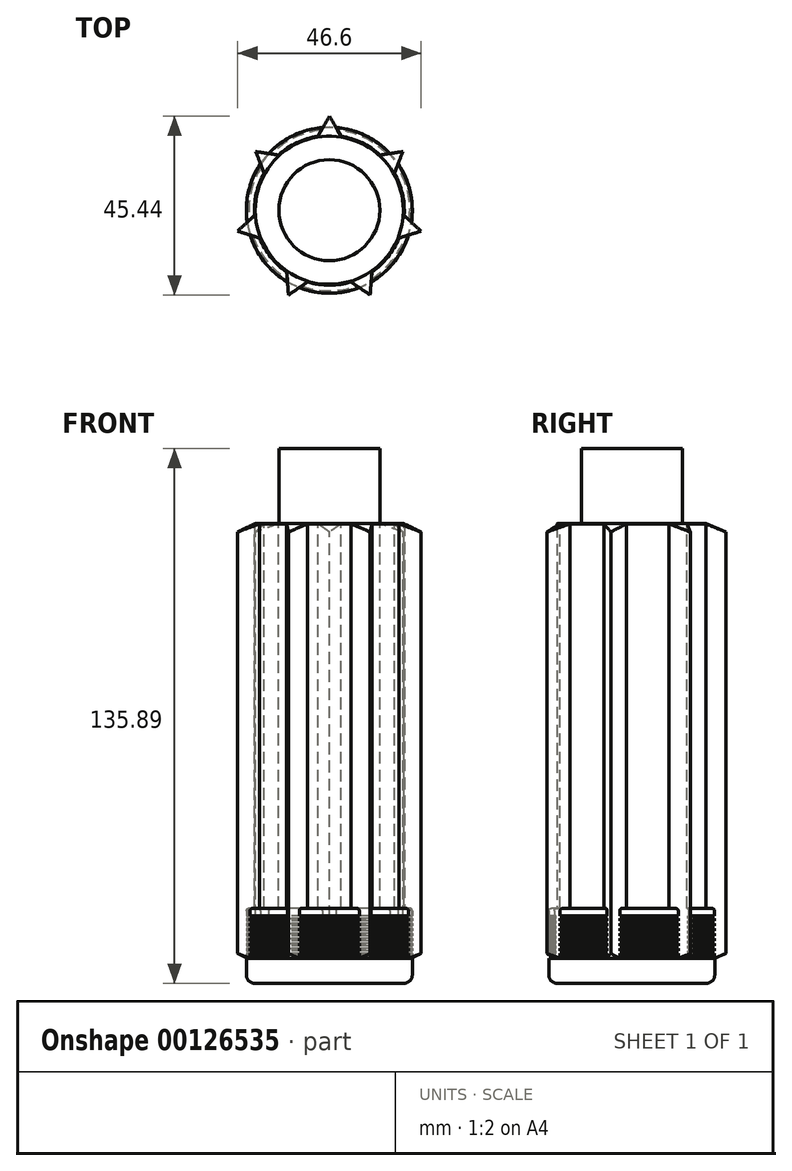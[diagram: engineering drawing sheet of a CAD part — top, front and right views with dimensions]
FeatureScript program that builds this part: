
annotation { "Feature Type Name" : "Feature", "Feature Type Description" : "" }
export const myFeature = defineFeature(function(context is Context, id is Id, definition is map)
    precondition{}
    {
        {
            var Q0;
            Q0=qCreatedBy(makeId("Top.planeOp"),FACE);
            var sketch = newSketch(context, id + "F0", { "sketchPlane" : qUnion([Q0])});
            skCircle(sketch, "E0", {"center": v(0, 0) * mm, "radius": 19.05 * mm});
            skSolve(sketch);
        }
        {
            var Q0;
            Q0 = qSketchRegion(id + "F0", true);
            extrude(context, id + "F1", {"entities" : qUnion([Q0]), "depth" : 116.84 * mm});
        }
        {
            var Q0;
            Q0=qCreatedBy(makeId("Top.planeOp"),FACE);
            var sketch = newSketch(context, id + "F2", { "sketchPlane" : qUnion([Q0])});
            skCircle(sketch, "E1.0", {"center": v(0, 0) * mm, "radius": 21.08 * mm});
            skSolve(sketch);
        }
        {
            var Q0;
            Q0 = qSketchRegion(id + "F2", true);
            extrude(context, id + "F3", {"entities" : qUnion([Q0]), "operationType" : NewBodyOperationType.ADD, "depth" : 19.05 * mm});
        }
        {
            var Q0;
            Q0=qCreatedBy(makeId("Front.planeOp"),FACE);
            var sketch = newSketch(context, id + "F4", { "sketchPlane" : qUnion([Q0])});
            skLineSegment(sketch, "E2.bottom", {"start": v(-21.08, 6.4) * mm, "end": v(-20.45, 6.4) * mm});
            skLineSegment(sketch, "E2.top", {"start": v(-21.08, 7.03) * mm, "end": v(-20.45, 7.03) * mm});
            skLineSegment(sketch, "E2.left", {"start": v(-21.08, 6.4) * mm, "end": v(-21.08, 7.03) * mm});
            skLineSegment(sketch, "E2.right", {"start": v(-20.45, 6.4) * mm, "end": v(-20.45, 7.03) * mm});
            skLineSegment(sketch, "E3.bottom", {"start": v(-21.08, 7.66) * mm, "end": v(-20.45, 7.66) * mm});
            skLineSegment(sketch, "E3.top", {"start": v(-21.08, 8.3) * mm, "end": v(-20.45, 8.3) * mm});
            skLineSegment(sketch, "E3.left", {"start": v(-21.08, 7.66) * mm, "end": v(-21.08, 8.3) * mm});
            skLineSegment(sketch, "E3.right", {"start": v(-20.45, 7.66) * mm, "end": v(-20.45, 8.3) * mm});
            skLineSegment(sketch, "E4.bottom", {"start": v(-21.08, 8.93) * mm, "end": v(-20.45, 8.93) * mm});
            skLineSegment(sketch, "E4.top", {"start": v(-21.08, 9.57) * mm, "end": v(-20.45, 9.57) * mm});
            skLineSegment(sketch, "E4.left", {"start": v(-21.08, 8.93) * mm, "end": v(-21.08, 9.57) * mm});
            skLineSegment(sketch, "E4.right", {"start": v(-20.45, 8.93) * mm, "end": v(-20.45, 9.57) * mm});
            skLineSegment(sketch, "E5.bottom", {"start": v(-21.08, 10.2) * mm, "end": v(-20.45, 10.2) * mm});
            skLineSegment(sketch, "E5.top", {"start": v(-21.08, 10.84) * mm, "end": v(-20.45, 10.84) * mm});
            skLineSegment(sketch, "E5.left", {"start": v(-21.08, 10.2) * mm, "end": v(-21.08, 10.84) * mm});
            skLineSegment(sketch, "E5.right", {"start": v(-20.45, 10.2) * mm, "end": v(-20.45, 10.84) * mm});
            skLineSegment(sketch, "E6.bottom", {"start": v(-21.08, 11.47) * mm, "end": v(-20.45, 11.47) * mm});
            skLineSegment(sketch, "E6.top", {"start": v(-21.08, 12.1) * mm, "end": v(-20.45, 12.1) * mm});
            skLineSegment(sketch, "E6.left", {"start": v(-21.08, 11.47) * mm, "end": v(-21.08, 12.1) * mm});
            skLineSegment(sketch, "E6.right", {"start": v(-20.45, 11.47) * mm, "end": v(-20.45, 12.1) * mm});
            skLineSegment(sketch, "E7", {"start": v(-21.08, 0) * mm, "end": v(-21.08, 28.76) * mm, "construction": true});
            skLineSegment(sketch, "E8", {"start": v(-25.98, 6.4) * mm, "end": v(29.05, 6.4) * mm, "construction": true});
            skLineSegment(sketch, "E9.bottom", {"start": v(-21.08, 12.74) * mm, "end": v(-20.45, 12.74) * mm});
            skLineSegment(sketch, "E9.top", {"start": v(-21.08, 13.38) * mm, "end": v(-20.45, 13.38) * mm});
            skLineSegment(sketch, "E9.right", {"start": v(-20.45, 12.74) * mm, "end": v(-20.45, 13.38) * mm});
            skLineSegment(sketch, "E10.bottom", {"start": v(-21.08, 14.01) * mm, "end": v(-20.45, 14.01) * mm});
            skLineSegment(sketch, "E10.top", {"start": v(-21.08, 14.65) * mm, "end": v(-20.45, 14.65) * mm});
            skLineSegment(sketch, "E10.right", {"start": v(-20.45, 14.01) * mm, "end": v(-20.45, 14.65) * mm});
            skLineSegment(sketch, "E11.bottom", {"start": v(-21.08, 15.28) * mm, "end": v(-20.45, 15.28) * mm});
            skLineSegment(sketch, "E11.top", {"start": v(-21.08, 15.92) * mm, "end": v(-20.45, 15.92) * mm});
            skLineSegment(sketch, "E11.right", {"start": v(-20.45, 15.28) * mm, "end": v(-20.45, 15.92) * mm});
            skLineSegment(sketch, "E12.bottom", {"start": v(-21.08, 16.55) * mm, "end": v(-20.45, 16.55) * mm});
            skLineSegment(sketch, "E12.top", {"start": v(-21.08, 17.19) * mm, "end": v(-20.45, 17.19) * mm});
            skLineSegment(sketch, "E12.right", {"start": v(-20.45, 16.55) * mm, "end": v(-20.45, 17.19) * mm});
            skLineSegment(sketch, "E13", {"start": v(-21.08, 16.55) * mm, "end": v(-21.08, 17.19) * mm});
            skLineSegment(sketch, "E14", {"start": v(-21.08, 12.74) * mm, "end": v(-21.08, 13.38) * mm});
            skLineSegment(sketch, "E15", {"start": v(-21.08, 14.01) * mm, "end": v(-21.08, 14.65) * mm});
            skLineSegment(sketch, "E16", {"start": v(-21.08, 15.28) * mm, "end": v(-21.08, 15.92) * mm});
            skLineSegment(sketch, "E17", {"start": v(0, 0) * mm, "end": v(0, 41.99) * mm, "construction": true});
            skSolve(sketch);
        }
        {
            var Q0;
            Q0 = qSketchRegion(id + "F4", true);
            var Q1;
            Q1=sQuery(id+"F4.wireOp",EDGE,"E17");
            revolve(context, id + "F5", {"operationType" : NewBodyOperationType.REMOVE, "entities" : qUnion([Q0]), "axis" : qUnion([Q1]), "revolveType" : RevolveType.FULL, "oppositeDirection" : true});
        }
        {
            var Q0;
            Q0=makeQuery(id+"F1.opExtrude","CAP_FACE",FACE,{"disambiguationData":[OSD([sQuery(id+"F0.wireOp",EDGE,"E0")])],"isStart":false});
            var sketch = newSketch(context, id + "F6", { "sketchPlane" : qUnion([Q0])});
            skCircle(sketch, "E18", {"center": v(0, 0) * mm, "radius": 12.82 * mm});
            skSolve(sketch);
        }
        {
            var Q0;
            Q0 = qSketchRegion(id + "F6", true);
            extrude(context, id + "F7", {"entities" : qUnion([Q0]), "operationType" : NewBodyOperationType.ADD, "depth" : 19.05 * mm});
        }
        {
            var Q0;
            Q0=makeQuery(id+"F1.opExtrude","CAP_FACE",FACE,{"disambiguationData":[OSD([sQuery(id+"F0.wireOp",EDGE,"E0")])],"isStart":false});
            var sketch = newSketch(context, id + "F8", { "sketchPlane" : qUnion([Q0])});
            skLineSegment(sketch, "E19", {"start": v(0, 23.9) * mm, "end": v(-2.93, 18.82) * mm});
            skLineSegment(sketch, "E20", {"start": v(-2.93, 18.82) * mm, "end": v(2.93, 18.82) * mm});
            skLineSegment(sketch, "E21", {"start": v(2.93, 18.82) * mm, "end": v(0, 23.9) * mm});
            skPoint(sketch, "E22.center", {"position": v(0, 0) * mm});
            skLineSegment(sketch, "E23.1.0", {"start": v(-12.89, 14.03) * mm, "end": v(-18.69, 14.9) * mm});
            skLineSegment(sketch, "E23.1.1", {"start": v(-16.54, 9.44) * mm, "end": v(-12.89, 14.03) * mm});
            skLineSegment(sketch, "E23.1.2", {"start": v(-18.69, 14.9) * mm, "end": v(-16.54, 9.44) * mm});
            skLineSegment(sketch, "E23.2.0", {"start": v(-19, -1.33) * mm, "end": v(-23.3, -5.32) * mm});
            skLineSegment(sketch, "E23.2.1", {"start": v(-17.7, -7.05) * mm, "end": v(-19, -1.33) * mm});
            skLineSegment(sketch, "E23.2.2", {"start": v(-23.3, -5.32) * mm, "end": v(-17.7, -7.05) * mm});
            skLineSegment(sketch, "E23.3.0", {"start": v(-10.8, -15.69) * mm, "end": v(-10.37, -21.54) * mm});
            skLineSegment(sketch, "E23.3.1", {"start": v(-5.52, -18.23) * mm, "end": v(-10.8, -15.69) * mm});
            skLineSegment(sketch, "E23.3.2", {"start": v(-10.37, -21.54) * mm, "end": v(-5.52, -18.23) * mm});
            skLineSegment(sketch, "E23.4.0", {"start": v(5.52, -18.23) * mm, "end": v(10.37, -21.54) * mm});
            skLineSegment(sketch, "E23.4.1", {"start": v(10.8, -15.69) * mm, "end": v(5.52, -18.23) * mm});
            skLineSegment(sketch, "E23.4.2", {"start": v(10.37, -21.54) * mm, "end": v(10.8, -15.69) * mm});
            skLineSegment(sketch, "E23.5.0", {"start": v(17.7, -7.05) * mm, "end": v(23.3, -5.32) * mm});
            skLineSegment(sketch, "E23.5.1", {"start": v(19, -1.33) * mm, "end": v(17.7, -7.05) * mm});
            skLineSegment(sketch, "E23.5.2", {"start": v(23.3, -5.32) * mm, "end": v(19, -1.33) * mm});
            skLineSegment(sketch, "E23.6.0", {"start": v(16.54, 9.44) * mm, "end": v(18.69, 14.9) * mm});
            skLineSegment(sketch, "E23.6.1", {"start": v(12.89, 14.03) * mm, "end": v(16.54, 9.44) * mm});
            skLineSegment(sketch, "E23.6.2", {"start": v(18.69, 14.9) * mm, "end": v(12.89, 14.03) * mm});
            skSolve(sketch);
        }
        {
            var Q0;
            Q0 = qSketchRegion(id + "F8", true);
            extrude(context, id + "F9", {"entities" : qUnion([Q0]), "operationType" : NewBodyOperationType.ADD, "oppositeDirection" : true, "depth" : 110.49 * mm});
        }
        {
            var Q0;
            Q0=qCreatedBy(makeId("Right.planeOp"),FACE);
            var sketch = newSketch(context, id + "F10", { "sketchPlane" : qUnion([Q0])});
            skLineSegment(sketch, "E24", {"start": v(18.82, 116.84) * mm, "end": v(23.9, 116.84) * mm});
            skLineSegment(sketch, "E25", {"start": v(23.9, 116.84) * mm, "end": v(23.9, 114.67) * mm});
            skLineSegment(sketch, "E26", {"start": v(23.9, 114.67) * mm, "end": v(18.82, 116.84) * mm});
            skLineSegment(sketch, "E27", {"start": v(21.02, 6.35) * mm, "end": v(23.9, 6.35) * mm});
            skLineSegment(sketch, "E28", {"start": v(23.9, 6.35) * mm, "end": v(23.9, 7.59) * mm});
            skLineSegment(sketch, "E29", {"start": v(23.9, 7.59) * mm, "end": v(21.02, 6.35) * mm});
            skLineSegment(sketch, "E30", {"start": v(0, 0) * mm, "end": v(0, 152.7) * mm, "construction": true});
            skSolve(sketch);
        }
        {
            var Q0;
            Q0 = qSketchRegion(id + "F10", true);
            var Q1;
            Q1=sQuery(id+"F10.wireOp",EDGE,"E30");
            revolve(context, id + "F11", {"operationType" : NewBodyOperationType.REMOVE, "entities" : qUnion([Q0]), "axis" : qUnion([Q1]), "revolveType" : RevolveType.FULL, "oppositeDirection" : true});
        }
        {
            var Q0;
            {var subQ0=sQuery(id+"F2.wireOp",EDGE,"E1.0");Q0=makeQuery(id+"F9.boolean.opBoolean","SPLIT",EDGE,{"disambiguationData":[TD([makeQuery(id+"F9.opExtrude","SWEPT_FACE",FACE,{"disambiguationData":[OSD([sQuery(id+"F8.wireOp",EDGE,"E21")])]})])],"derivedFrom":makeQuery(id+"F3.opExtrude","CAP_EDGE",EDGE,{"disambiguationData":[OSD([subQ0])],"isStart":false})});}
            var Q1;
            {var subQ0=sQuery(id+"F2.wireOp",EDGE,"E1.0");Q1=makeQuery(id+"F9.boolean.opBoolean","SPLIT",EDGE,{"disambiguationData":[TD([makeQuery(id+"F9.opExtrude","SWEPT_FACE",FACE,{"disambiguationData":[OSD([sQuery(id+"F8.wireOp",EDGE,"E19")])]})])],"derivedFrom":makeQuery(id+"F3.opExtrude","CAP_EDGE",EDGE,{"disambiguationData":[OSD([subQ0])],"isStart":false})});}
            var Q2;
            {var subQ0=sQuery(id+"F2.wireOp",EDGE,"E1.0");Q2=makeQuery(id+"F9.boolean.opBoolean","SPLIT",EDGE,{"disambiguationData":[TD([makeQuery(id+"F9.opExtrude","SWEPT_FACE",FACE,{"disambiguationData":[OSD([sQuery(id+"F8.wireOp",EDGE,"E23.1.2")])]})])],"derivedFrom":makeQuery(id+"F3.opExtrude","CAP_EDGE",EDGE,{"disambiguationData":[OSD([subQ0])],"isStart":false})});}
            var Q3;
            {var subQ0=sQuery(id+"F2.wireOp",EDGE,"E1.0");Q3=makeQuery(id+"F9.boolean.opBoolean","SPLIT",EDGE,{"disambiguationData":[TD([makeQuery(id+"F9.opExtrude","SWEPT_FACE",FACE,{"disambiguationData":[OSD([sQuery(id+"F8.wireOp",EDGE,"E23.2.2")])]})])],"derivedFrom":makeQuery(id+"F3.opExtrude","CAP_EDGE",EDGE,{"disambiguationData":[OSD([subQ0])],"isStart":false})});}
            var Q4;
            {var subQ0=sQuery(id+"F2.wireOp",EDGE,"E1.0");Q4=makeQuery(id+"F9.boolean.opBoolean","SPLIT",EDGE,{"disambiguationData":[TD([makeQuery(id+"F9.opExtrude","SWEPT_FACE",FACE,{"disambiguationData":[OSD([sQuery(id+"F8.wireOp",EDGE,"E23.3.2")])]})])],"derivedFrom":makeQuery(id+"F3.opExtrude","CAP_EDGE",EDGE,{"disambiguationData":[OSD([subQ0])],"isStart":false})});}
            var Q5;
            {var subQ0=sQuery(id+"F2.wireOp",EDGE,"E1.0");Q5=makeQuery(id+"F9.boolean.opBoolean","SPLIT",EDGE,{"disambiguationData":[TD([makeQuery(id+"F9.opExtrude","SWEPT_FACE",FACE,{"disambiguationData":[OSD([sQuery(id+"F8.wireOp",EDGE,"E23.4.2")])]})])],"derivedFrom":makeQuery(id+"F3.opExtrude","CAP_EDGE",EDGE,{"disambiguationData":[OSD([subQ0])],"isStart":false})});}
            var Q6;
            {var subQ0=sQuery(id+"F2.wireOp",EDGE,"E1.0");Q6=makeQuery(id+"F9.boolean.opBoolean","SPLIT",EDGE,{"disambiguationData":[TD([makeQuery(id+"F9.opExtrude","SWEPT_FACE",FACE,{"disambiguationData":[OSD([sQuery(id+"F8.wireOp",EDGE,"E23.5.2")])]})])],"derivedFrom":makeQuery(id+"F3.opExtrude","CAP_EDGE",EDGE,{"disambiguationData":[OSD([subQ0])],"isStart":false})});}
            fillet(context, id + "F12", {"entities" : qUnion([Q0, Q1, Q2, Q3, Q4, Q5, Q6]), "radius" : 0.62 * mm, "tangentPropagation" : true, "allowEdgeOverflow" : false});
        }
        {
            var Q0;
            Q0=makeQuery(id+"F3.opExtrude","CAP_EDGE",EDGE,{"disambiguationData":[OSD([sQuery(id+"F2.wireOp",EDGE,"E1.0")])],"isStart":true});
            fillet(context, id + "F13", {"entities" : qUnion([Q0]), "radius" : 2.15 * mm, "tangentPropagation" : true, "allowEdgeOverflow" : false});
        }
    });
